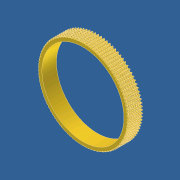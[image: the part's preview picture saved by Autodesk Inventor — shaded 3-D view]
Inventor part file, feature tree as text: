
AUTODESK INVENTOR PART (.ipt)
format: ipt  version: 2011 (Build 150239000, 239)  size: 6,426,112 bytes
history: native  units: in
note: dims shown in document units (in); Inventor stores cm internally (conversion verified against a paired STEP export)
features: extrude x2, sketch x2, pattern_circular x1, pattern_linear x1
ambient origin geometry x8: Origin, YZ Plane, XZ Plane, XY Plane, X Axis, Y Axis, Z Axis, Center Point
bodies: Solid1 (feature_tree)
feature tree (6):
  extrude  "Extrusion1"  Depth=0.05in
  extrude  "Extrusion2"  Depth=0.0714in TaperAngle=0.0deg
  pattern_circular  "Circular Pattern2"  [2 undecoded]
  pattern_linear  "Rectangular Pattern1"  Spacing1=0.0754in  [1 undecoded]
  sketch  "Sketch1"  dims[d1=0.05in d2=0.05in]
  sketch  "Sketch2"  dims[d3=3.067in d4=0.0714in d5=0.0in d6=0.292in d7=0.0754in d9=0.0754in d10=0.0714in d11=0.0in d15=37.7953in d16=360.0deg d18=2.7559in d20=0.1429in d22=0.0258in]
note: 3 required parameter values undecoded (feature->parameter linkage not recoverable at this tier; creation-order binding heuristic only, values carry confidence <= 0.55)
